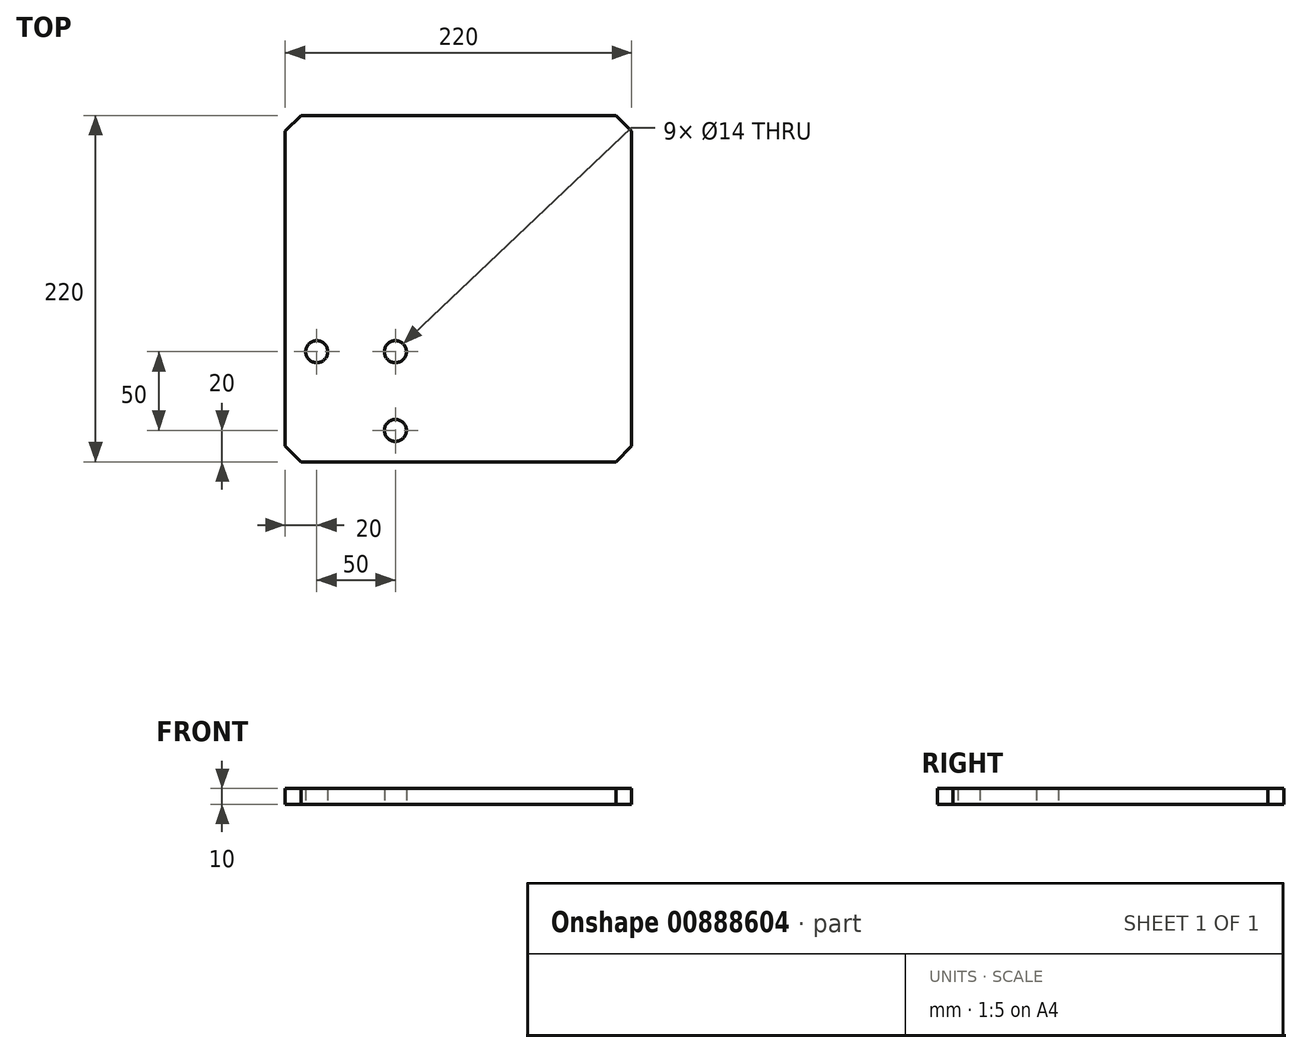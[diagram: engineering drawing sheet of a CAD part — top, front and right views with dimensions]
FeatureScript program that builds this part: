
annotation { "Feature Type Name" : "Feature", "Feature Type Description" : "" }
export const myFeature = defineFeature(function(context is Context, id is Id, definition is map)
    precondition{}
    {
        {
            var Q0;
            Q0=qCreatedBy(makeId("Top.planeOp"),FACE);
            var sketch = newSketch(context, id + "F0", { "sketchPlane" : qUnion([Q0])});
            skLineSegment(sketch, "E0.bottom", {"start": v(0, 0) * mm, "end": v(220, 0) * mm});
            skLineSegment(sketch, "E0.top", {"start": v(0, 220) * mm, "end": v(220, 220) * mm});
            skLineSegment(sketch, "E0.left", {"start": v(0, 0) * mm, "end": v(0, 220) * mm});
            skLineSegment(sketch, "E0.right", {"start": v(220, 0) * mm, "end": v(220, 220) * mm});
            skLineSegment(sketch, "E1.0", {"start": v(0, 140) * mm, "end": v(140, 140) * mm, "construction": true});
            skLineSegment(sketch, "E2.0", {"start": v(140, 0) * mm, "end": v(140, 140) * mm, "construction": true});
            skLineSegment(sketch, "E3", {"start": v(140, 70) * mm, "end": v(0, 70) * mm, "construction": true});
            skPoint(sketch, "E3.endSnap0", {"position": v(140, 70) * mm});
            skLineSegment(sketch, "E4", {"start": v(70, 140) * mm, "end": v(70, 0) * mm, "construction": true});
            skLineSegment(sketch, "E5", {"start": v(0, 270) * mm, "end": v(270, 270) * mm, "construction": true});
            skLineSegment(sketch, "E6", {"start": v(270, 270) * mm, "end": v(270, 0) * mm, "construction": true});
            skCircle(sketch, "E7", {"center": v(20, 70) * mm, "radius": 7 * mm});
            skCircle(sketch, "E8", {"center": v(70, 70) * mm, "radius": 7 * mm});
            skCircle(sketch, "E9", {"center": v(70, 20) * mm, "radius": 7 * mm});
            skLineSegment(sketch, "E10.bottom", {"start": v(270, 270) * mm, "end": v(70, 270) * mm, "construction": true});
            skLineSegment(sketch, "E10.top", {"start": v(270, 70) * mm, "end": v(70, 70) * mm, "construction": true});
            skLineSegment(sketch, "E10.left", {"start": v(270, 270) * mm, "end": v(270, 70) * mm, "construction": true});
            skLineSegment(sketch, "E10.right", {"start": v(70, 270) * mm, "end": v(70, 70) * mm, "construction": true});
            skSolve(sketch);
        }
        {
            var Q0;
            Q0=makeQuery(id+"F0.imprint","IMPRINT",FACE,{"disambiguationData":[TD([[makeQuery(id+"F0.imprint","IMPRINT",EDGE,{"derivedFrom":sQuery(id+"F0.wireOp",EDGE,"E0.bottom")}),1.0]])]});
            extrude(context, id + "F1", {"entities" : qUnion([Q0]), "depth" : 10 * mm, "offsetDistance" : 25 * mm});
        }
        {
            var Q0;
            Q0=makeQuery(id+"F1.opExtrude","SWEPT_EDGE",EDGE,{"disambiguationData":[OSD([sQuery(id+"F0.wireOp",EDGE,"E0.top"),sQuery(id+"F0.wireOp",EDGE,"E0.left")])]});
            var Q1;
            Q1=makeQuery(id+"F1.opExtrude","SWEPT_EDGE",EDGE,{"disambiguationData":[OSD([sQuery(id+"F0.wireOp",EDGE,"E0.bottom"),sQuery(id+"F0.wireOp",EDGE,"E0.left")])]});
            var Q2;
            Q2=makeQuery(id+"F1.opExtrude","SWEPT_EDGE",EDGE,{"disambiguationData":[OSD([sQuery(id+"F0.wireOp",EDGE,"E0.bottom"),sQuery(id+"F0.wireOp",EDGE,"E0.right")])]});
            var Q3;
            Q3=makeQuery(id+"F1.opExtrude","SWEPT_EDGE",EDGE,{"disambiguationData":[OSD([sQuery(id+"F0.wireOp",EDGE,"E0.top"),sQuery(id+"F0.wireOp",EDGE,"E0.right")])]});
            chamfer(context, id + "F2", {"entities" : qUnion([Q0, Q1, Q2, Q3]), "width" : 10 * mm, "tangentPropagation" : true});
        }
    });
